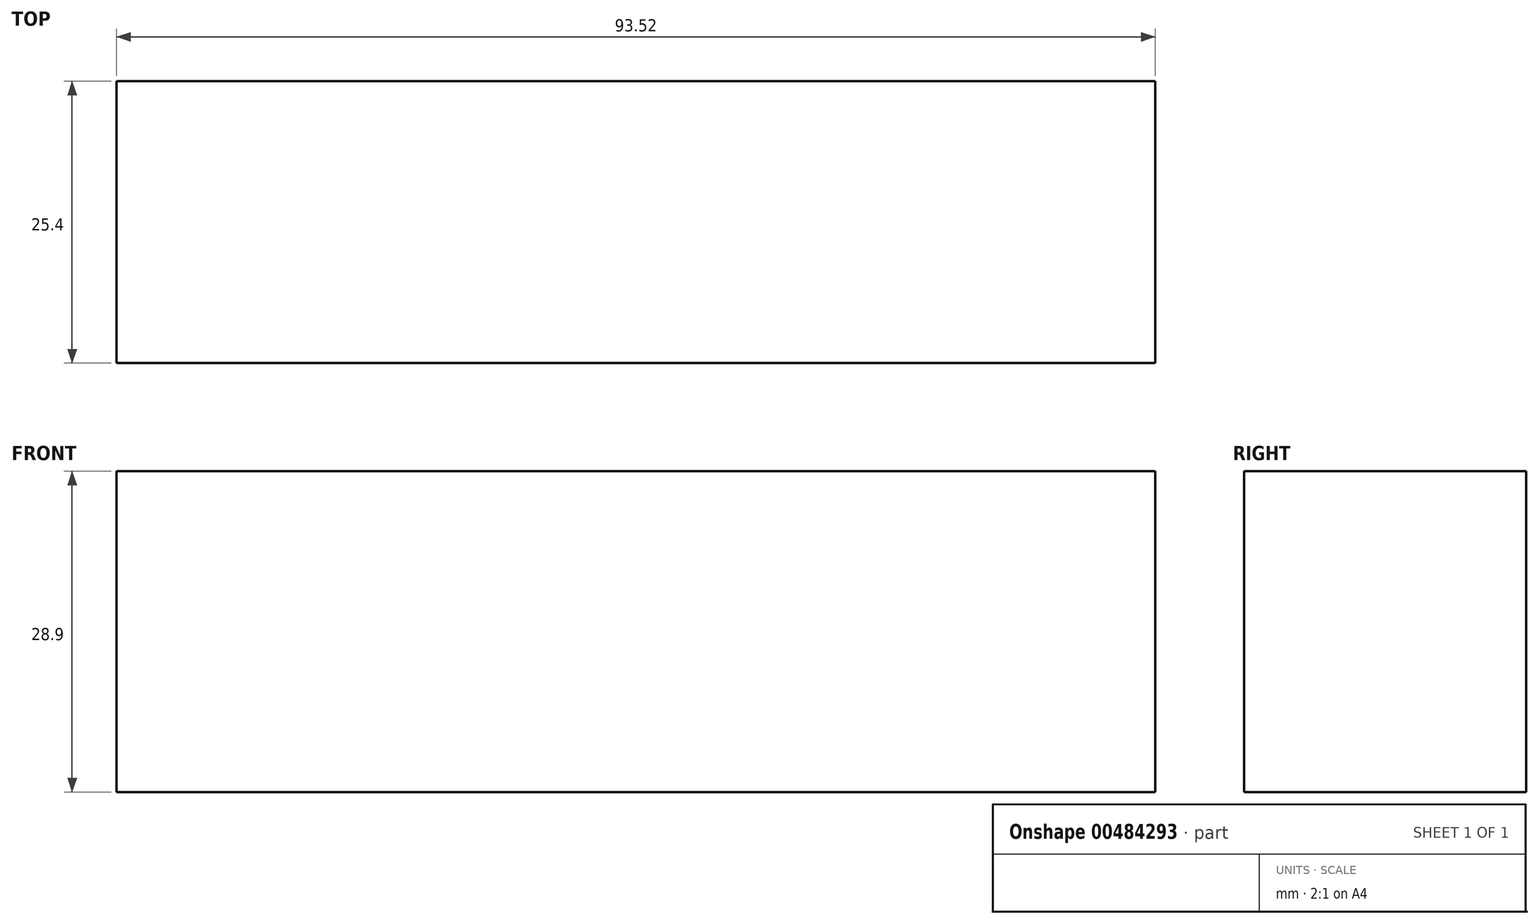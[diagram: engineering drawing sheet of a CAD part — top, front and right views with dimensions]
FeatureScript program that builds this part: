
annotation { "Feature Type Name" : "Feature", "Feature Type Description" : "" }
export const myFeature = defineFeature(function(context is Context, id is Id, definition is map)
    precondition{}
    {
        {
            var Q0;
            Q0=qCreatedBy(makeId("Front.planeOp"),FACE);
            var sketch = newSketch(context, id + "F0", { "sketchPlane" : qUnion([Q0])});
            skLineSegment(sketch, "E0.bottom", {"start": v(-46.76, 14.45) * mm, "end": v(46.76, 14.45) * mm});
            skLineSegment(sketch, "E0.top", {"start": v(-46.76, -14.45) * mm, "end": v(46.76, -14.45) * mm});
            skLineSegment(sketch, "E0.left", {"start": v(-46.76, 14.45) * mm, "end": v(-46.76, -14.45) * mm});
            skLineSegment(sketch, "E0.right", {"start": v(46.76, 14.45) * mm, "end": v(46.76, -14.45) * mm});
            skPoint(sketch, "E0.middle", {"position": v(0, 0) * mm});
            skSolve(sketch);
        }
        {
            var Q0;
            Q0=makeQuery(id+"F0.imprint","IMPRINT",FACE,{"disambiguationData":[TD([[makeQuery(id+"F0.imprint","IMPRINT",EDGE,{"derivedFrom":sQuery(id+"F0.wireOp",EDGE,"E0.bottom")}),-1.0]])]});
            extrude(context, id + "F1", {"entities" : qUnion([Q0]), "depth" : 25.4 * mm});
        }
    });
